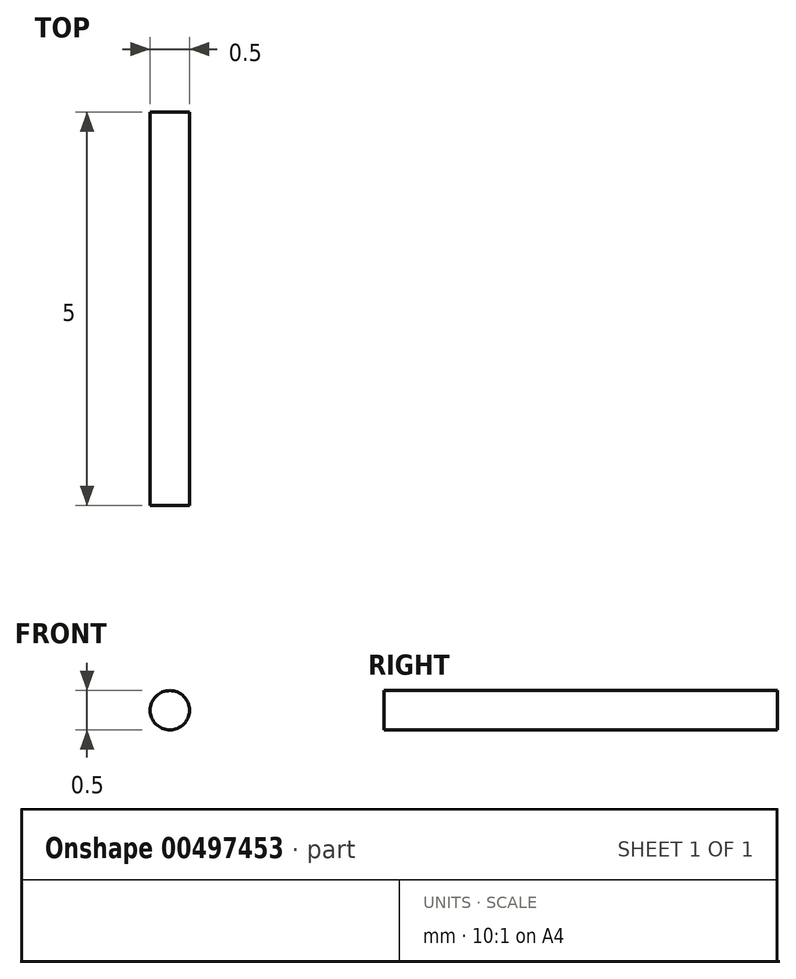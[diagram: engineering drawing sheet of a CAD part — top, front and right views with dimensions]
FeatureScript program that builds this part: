
annotation { "Feature Type Name" : "Feature", "Feature Type Description" : "" }
export const myFeature = defineFeature(function(context is Context, id is Id, definition is map)
    precondition{}
    {
        {
            var Q0;
            Q0=qCreatedBy(makeId("Front.planeOp"),FACE);
            var sketch = newSketch(context, id + "F0", { "sketchPlane" : qUnion([Q0])});
            skCircle(sketch, "E0", {"center": v(0, 0) * mm, "radius": 0.25 * mm});
            skSolve(sketch);
        }
        {
            var Q0;
            Q0 = qSketchRegion(id + "F0", true);
            extrude(context, id + "F1", {"entities" : qUnion([Q0]), "depth" : 5 * mm});
        }
    });
